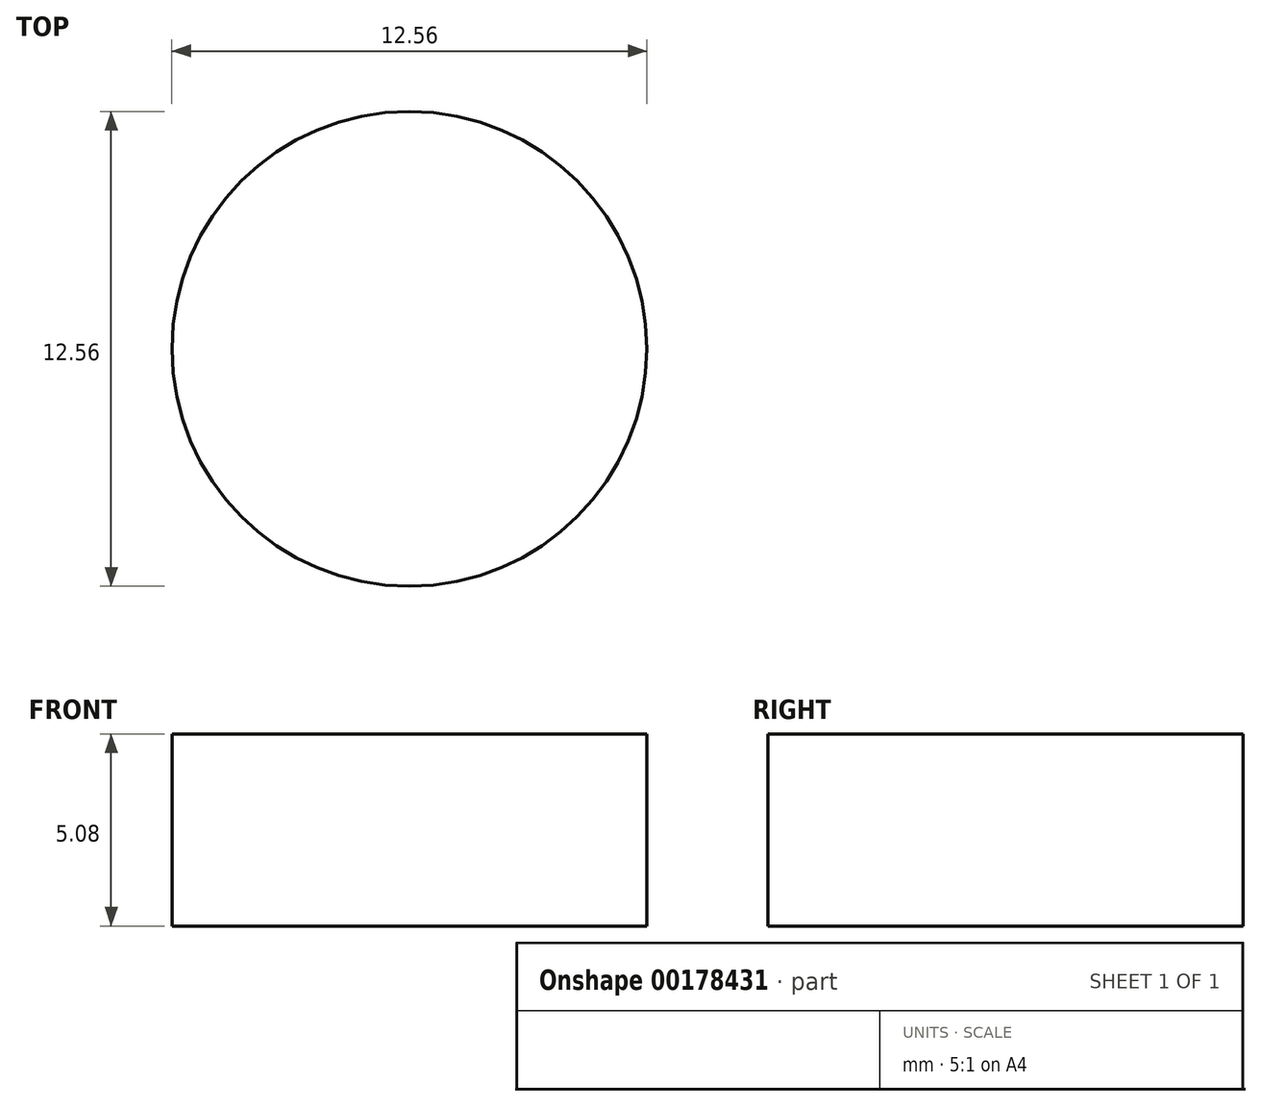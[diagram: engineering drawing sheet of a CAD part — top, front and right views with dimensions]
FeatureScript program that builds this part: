
annotation { "Feature Type Name" : "Feature", "Feature Type Description" : "" }
export const myFeature = defineFeature(function(context is Context, id is Id, definition is map)
    precondition{}
    {
        {
            var Q0;
            Q0=qCreatedBy(makeId("Top.planeOp"),FACE);
            var sketch = newSketch(context, id + "F0", { "sketchPlane" : qUnion([Q0])});
            skCircle(sketch, "E0", {"center": v(0, 0) * mm, "radius": 6.28 * mm});
            skSolve(sketch);
        }
        {
            var Q0;
            Q0=makeQuery(id+"F0.imprint","IMPRINT",FACE,{"disambiguationData":[TD([[makeQuery(id+"F0.imprint","IMPRINT",EDGE,{"derivedFrom":sQuery(id+"F0.wireOp",EDGE,"E0")}),1.0]])]});
            extrude(context, id + "F1", {"entities" : qUnion([Q0]), "depth" : 5.08 * mm});
        }
    });
